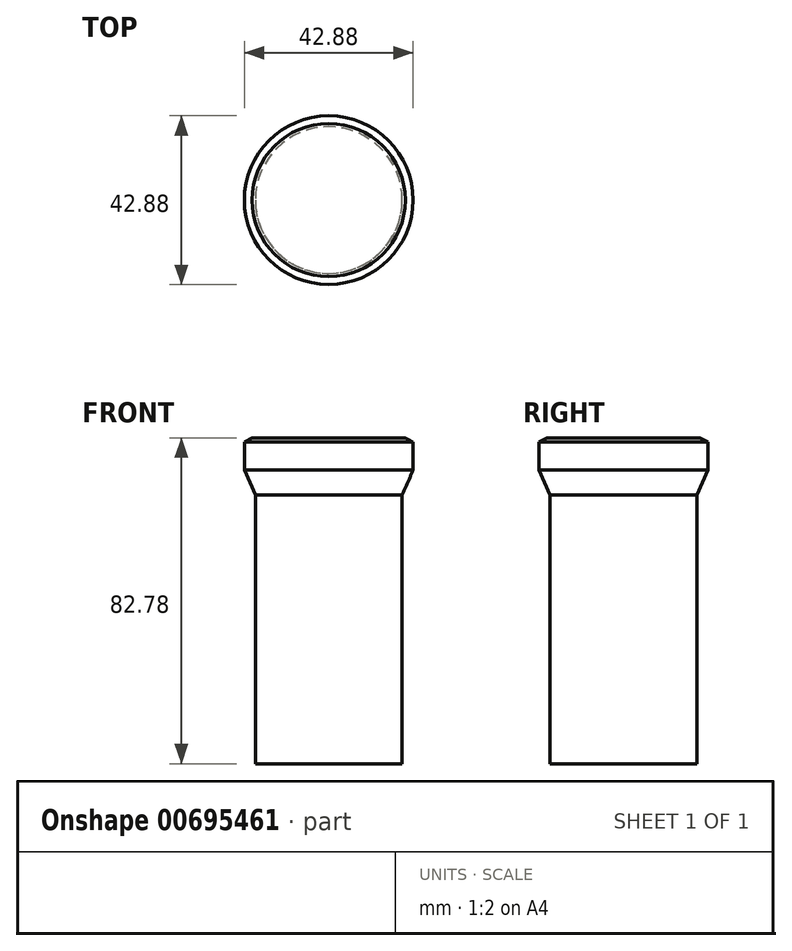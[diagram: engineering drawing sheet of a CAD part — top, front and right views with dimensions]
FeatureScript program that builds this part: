
annotation { "Feature Type Name" : "Feature", "Feature Type Description" : "" }
export const myFeature = defineFeature(function(context is Context, id is Id, definition is map)
    precondition{}
    {
        {
            var Q0;
            Q0=qCreatedBy(makeId("Top.planeOp"),FACE);
            var sketch = newSketch(context, id + "F0", { "sketchPlane" : qUnion([Q0])});
            skCircle(sketch, "E0", {"center": v(0, 0) * mm, "radius": 19.44 * mm});
            skSolve(sketch);
        }
        {
            var Q0;
            Q0=qCreatedBy(makeId("Top.planeOp"),FACE);
            cPlane(context, id + "F1", {"entities" : qUnion([Q0]), "cplaneType" : CPlaneType.OFFSET, "offset" : 1.07 * mm, "oppositeDirection" : true, "width" : 152.4 * mm, "height" : 152.4 * mm});
        }
        {
            var Q0;
            Q0=qCreatedBy(id+"F1.planeOp",FACE);
            var sketch = newSketch(context, id + "F2", { "sketchPlane" : qUnion([Q0])});
            skCircle(sketch, "E1", {"center": v(0, 0) * mm, "radius": 21.44 * mm});
            skSolve(sketch);
        }
        {
            var Q0;
            Q0=makeQuery(id+"F0.imprint","IMPRINT",FACE,{"disambiguationData":[TD([[makeQuery(id+"F0.imprint","IMPRINT",EDGE,{"derivedFrom":sQuery(id+"F0.wireOp",EDGE,"E0")}),1.0]])]});
            var Q1;
            Q1=makeQuery(id+"F2.imprint","IMPRINT",FACE,{"disambiguationData":[TD([[makeQuery(id+"F2.imprint","IMPRINT",EDGE,{"derivedFrom":sQuery(id+"F2.wireOp",EDGE,"E1")}),1.0]])]});
            loft(context, id + "F3", {"sheetProfilesArray" : [{ "sheetProfileEntities" : qUnion([Q0]) }, { "sheetProfileEntities" : qUnion([Q1]) }]});
        }
        {
            var Q0;
            Q0=makeQuery(id+"F3.opLoft","CAP_FACE",FACE,{"disambiguationData":[OSD([makeQuery(id+"F2.imprint","IMPRINT",FACE,{"disambiguationData":[TD([[makeQuery(id+"F2.imprint","IMPRINT",EDGE,{"derivedFrom":sQuery(id+"F2.wireOp",EDGE,"E1")}),1.0]])]})])],"isStart":true});
            extrude(context, id + "F4", {"entities" : qUnion([Q0]), "operationType" : NewBodyOperationType.ADD, "depth" : 7.1 * mm, "offsetDistance" : 25.4 * mm});
        }
        {
            var Q0;
            Q0=makeQuery(id+"F4.opExtrude","CAP_FACE",FACE,{"disambiguationData":[OSD([makeQuery(id+"F2.imprint","IMPRINT",FACE,{"disambiguationData":[TD([[makeQuery(id+"F2.imprint","IMPRINT",EDGE,{"derivedFrom":sQuery(id+"F2.wireOp",EDGE,"E1")}),1.0]])]})])],"isStart":false});
            cPlane(context, id + "F5", {"entities" : qUnion([Q0]), "cplaneType" : CPlaneType.OFFSET, "offset" : 6.35 * mm, "width" : 152.4 * mm, "height" : 152.4 * mm});
        }
        {
            var Q0;
            Q0=qCreatedBy(id+"F5.planeOp",FACE);
            var sketch = newSketch(context, id + "F6", { "sketchPlane" : qUnion([Q0])});
            skCircle(sketch, "E2", {"center": v(0, 0) * mm, "radius": 18.66 * mm});
            skSolve(sketch);
        }
        {
            var Q0;
            Q0=makeQuery(id+"F4.opExtrude","CAP_FACE",FACE,{"disambiguationData":[OSD([makeQuery(id+"F2.imprint","IMPRINT",FACE,{"disambiguationData":[TD([[makeQuery(id+"F2.imprint","IMPRINT",EDGE,{"derivedFrom":sQuery(id+"F2.wireOp",EDGE,"E1")}),1.0]])]})])],"isStart":false});
            var Q1;
            Q1=makeQuery(id+"F6.imprint","IMPRINT",FACE,{"disambiguationData":[TD([[makeQuery(id+"F6.imprint","IMPRINT",EDGE,{"derivedFrom":sQuery(id+"F6.wireOp",EDGE,"E2")}),1.0]])]});
            loft(context, id + "F7", {"operationType" : NewBodyOperationType.ADD, "sheetProfilesArray" : [{ "sheetProfileEntities" : qUnion([Q0]) }, { "sheetProfileEntities" : qUnion([Q1]) }]});
        }
        {
            var Q0;
            Q0=makeQuery(id+"F7.opLoft","CAP_FACE",FACE,{"disambiguationData":[OSD([makeQuery(id+"F6.imprint","IMPRINT",FACE,{"disambiguationData":[TD([[makeQuery(id+"F6.imprint","IMPRINT",EDGE,{"derivedFrom":sQuery(id+"F6.wireOp",EDGE,"E2")}),1.0]])]})])],"isStart":true});
            extrude(context, id + "F8", {"entities" : qUnion([Q0]), "depth" : 68.28 * mm, "offsetDistance" : 25.4 * mm});
        }
    });
